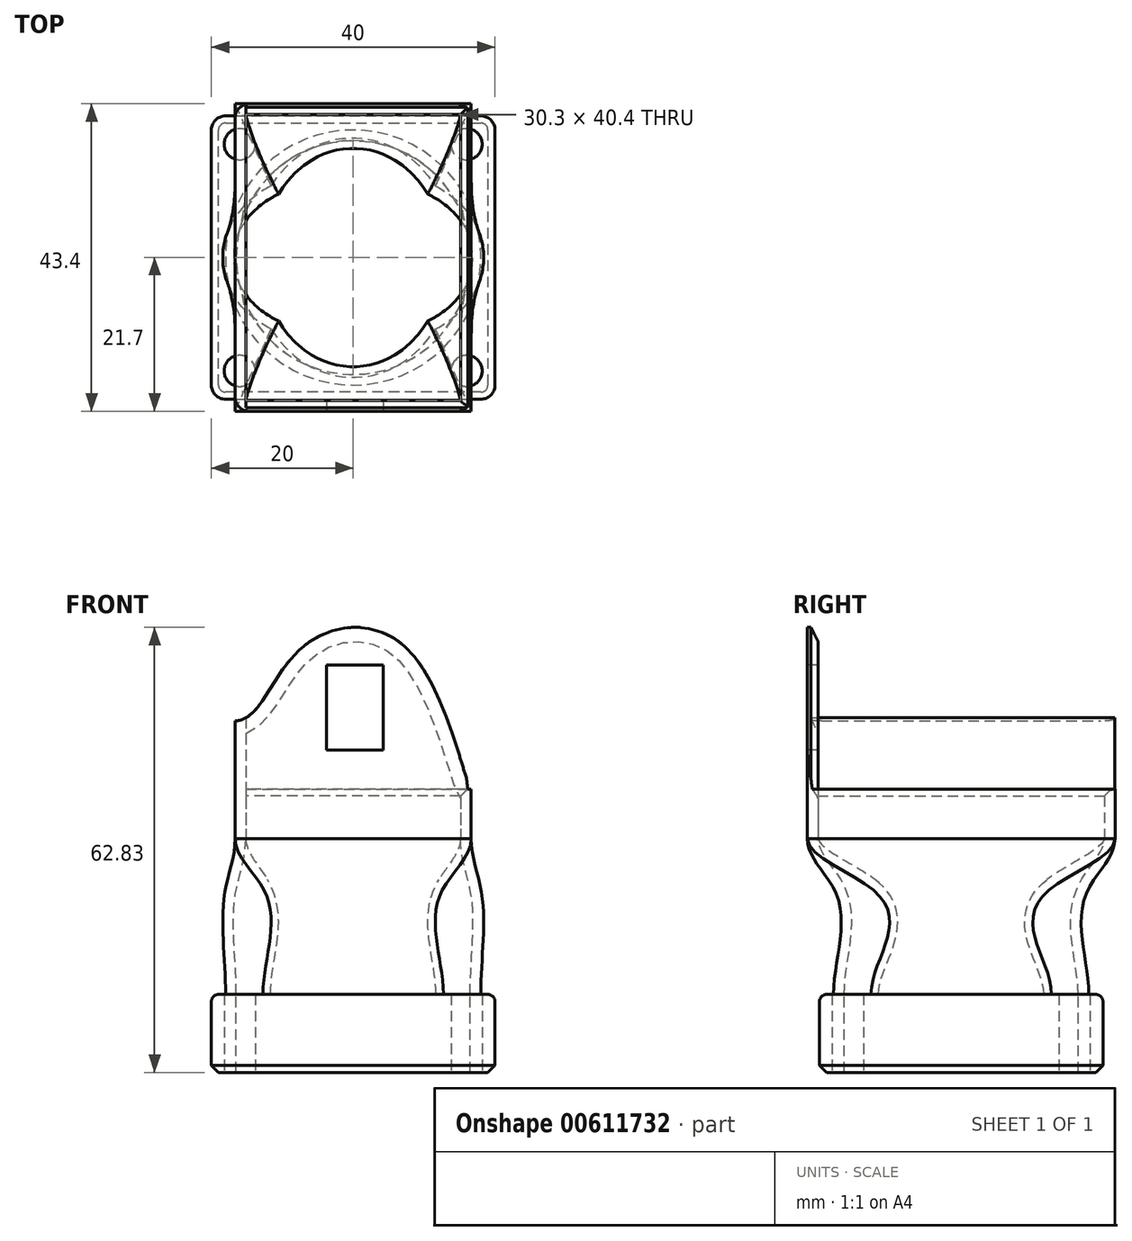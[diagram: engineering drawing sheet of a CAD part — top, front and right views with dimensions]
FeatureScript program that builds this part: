
annotation { "Feature Type Name" : "Feature", "Feature Type Description" : "" }
export const myFeature = defineFeature(function(context is Context, id is Id, definition is map)
    precondition{}
    {
        {
            var Q0;
            Q0=qCreatedBy(makeId("Top.planeOp"),FACE);
            var sketch = newSketch(context, id + "F0", { "sketchPlane" : qUnion([Q0])});
            skLineSegment(sketch, "E0.bottom", {"start": v(-15.15, 20.2) * mm, "end": v(15.15, 20.2) * mm});
            skLineSegment(sketch, "E0.top", {"start": v(-15.15, -20.2) * mm, "end": v(15.15, -20.2) * mm});
            skLineSegment(sketch, "E0.left", {"start": v(-15.15, 20.2) * mm, "end": v(-15.15, -20.2) * mm});
            skLineSegment(sketch, "E0.right", {"start": v(15.15, 20.2) * mm, "end": v(15.15, -20.2) * mm});
            skPoint(sketch, "E0.middle", {"position": v(0, 0) * mm});
            skSolve(sketch);
        }
        {
            var Q0;
            Q0=qCreatedBy(makeId("Top.planeOp"),FACE);
            var sketch = newSketch(context, id + "F1", { "sketchPlane" : qUnion([Q0])});
            skLineSegment(sketch, "E1.0", {"start": v(16.65, 21.7) * mm, "end": v(-16.65, 21.7) * mm});
            skLineSegment(sketch, "E1.1", {"start": v(16.65, -21.7) * mm, "end": v(16.65, 21.7) * mm});
            skLineSegment(sketch, "E1.2", {"start": v(-16.65, -21.7) * mm, "end": v(16.65, -21.7) * mm});
            skLineSegment(sketch, "E1.3", {"start": v(-16.65, 21.7) * mm, "end": v(-16.65, -21.7) * mm});
            skSolve(sketch);
        }
        {
            var Q0;
            Q0=qCreatedBy(makeId("Top.planeOp"),FACE);
            cPlane(context, id + "F2", {"entities" : qUnion([Q0]), "cplaneType" : CPlaneType.OFFSET, "offset" : 22 * mm, "oppositeDirection" : true, "width" : 150 * mm, "height" : 150 * mm});
        }
        {
            var Q0;
            Q0=qCreatedBy(id+"F2.planeOp",FACE);
            var sketch = newSketch(context, id + "F3", { "sketchPlane" : qUnion([Q0])});
            skCircle(sketch, "E2", {"center": v(0, 0) * mm, "radius": 18 * mm});
            skLineSegment(sketch, "E3.bottom", {"start": v(12.73, 12.73) * mm, "end": v(-12.73, 12.73) * mm, "construction": true});
            skLineSegment(sketch, "E3.top", {"start": v(12.73, -12.73) * mm, "end": v(-12.73, -12.73) * mm, "construction": true});
            skLineSegment(sketch, "E3.left", {"start": v(12.73, 12.73) * mm, "end": v(12.73, -12.73) * mm, "construction": true});
            skLineSegment(sketch, "E3.right", {"start": v(-12.73, 12.73) * mm, "end": v(-12.73, -12.73) * mm, "construction": true});
            skSolve(sketch);
        }
        {
            var Q0;
            Q0=qCreatedBy(id+"F2.planeOp",FACE);
            cPlane(context, id + "F4", {"entities" : qUnion([Q0]), "cplaneType" : CPlaneType.OFFSET, "offset" : 15 * mm, "width" : 150 * mm, "height" : 150 * mm});
        }
        {
            var Q0;
            Q0=qCreatedBy(id+"F4.planeOp",FACE);
            var sketch = newSketch(context, id + "F5", { "sketchPlane" : qUnion([Q0])});
            skCircle(sketch, "E4.0", {"center": v(0, 0) * mm, "radius": 18 * mm});
            skLineSegment(sketch, "E5.bottom", {"start": v(12.73, 12.73) * mm, "end": v(-12.73, 12.73) * mm, "construction": true});
            skLineSegment(sketch, "E5.top", {"start": v(12.73, -12.73) * mm, "end": v(-12.73, -12.73) * mm, "construction": true});
            skLineSegment(sketch, "E5.left", {"start": v(12.73, 12.73) * mm, "end": v(12.73, -12.73) * mm, "construction": true});
            skLineSegment(sketch, "E5.right", {"start": v(-12.73, 12.73) * mm, "end": v(-12.73, -12.73) * mm, "construction": true});
            skSolve(sketch);
        }
        {
            var Q0;
            Q0=makeQuery(id+"F1.imprint","IMPRINT",FACE,{"disambiguationData":[TD([[makeQuery(id+"F1.imprint","IMPRINT",EDGE,{"derivedFrom":sQuery(id+"F1.wireOp",EDGE,"E1.0")}),1.0]])]});
            var Q1;
            Q1=makeQuery(id+"F5.imprint","IMPRINT",FACE,{"disambiguationData":[TD([[makeQuery(id+"F5.imprint","IMPRINT",EDGE,{"derivedFrom":sQuery(id+"F5.wireOp",EDGE,"E4.0")}),1.0]])]});
            var Q2;
            Q2=makeQuery(id+"F3.imprint","IMPRINT",FACE,{"disambiguationData":[TD([[makeQuery(id+"F3.imprint","IMPRINT",EDGE,{"derivedFrom":sQuery(id+"F3.wireOp",EDGE,"E2")}),1.0]])]});
            var Q3;
            Q3=sQuery(id+"F1.wireOp",VERTEX,"E1.1.end");
            var Q4;
            Q4=sQuery(id+"F5.wireOp",VERTEX,"E5.bottom.start");
            var Q5;
            Q5=sQuery(id+"F3.wireOp",VERTEX,"E3.left.start");
            loft(context, id + "F6", {"startCondition" : LoftEndDerivativeType.NORMAL_TO_PROFILE, "startMagnitude" : 1, "endCondition" : LoftEndDerivativeType.NORMAL_TO_PROFILE, "endMagnitude" : 1, "sheetProfilesArray" : [{ "sheetProfileEntities" : qUnion([Q0]) }, { "sheetProfileEntities" : qUnion([Q1]) }, { "sheetProfileEntities" : qUnion([Q2]) }], "matchConnections" : true, "connections" : [{ "connectionEntities" : qUnion([Q3, Q4, Q5]), "connectionEdgeQueries" : qUnion([]), "connectionEdgeParameters" : [] }]});
        }
        {
            var Q0;
            Q0=makeQuery(id+"F6.opLoft","CAP_FACE",FACE,{"disambiguationData":[OSD([makeQuery(id+"F1.imprint","IMPRINT",FACE,{"disambiguationData":[TD([[makeQuery(id+"F1.imprint","IMPRINT",EDGE,{"derivedFrom":sQuery(id+"F1.wireOp",EDGE,"E1.0")}),1.0]])]})])],"isStart":true});
            var Q1;
            Q1=makeQuery(id+"F6.opLoft","CAP_FACE",FACE,{"disambiguationData":[OSD([makeQuery(id+"F3.imprint","IMPRINT",FACE,{"disambiguationData":[TD([[makeQuery(id+"F3.imprint","IMPRINT",EDGE,{"derivedFrom":sQuery(id+"F3.wireOp",EDGE,"E2")}),1.0]])]})])],"isStart":true});
            shell(context, id + "F7", {"entities" : qUnion([Q0, Q1]), "thickness" : 1.5 * mm});
        }
        {
            var Q0;
            Q0=qSketchRegion(id+"F1",true);
            extrude(context, id + "F8", {"entities" : qUnion([Q0]), "depth" : 7 * mm});
        }
        {
            var Q0;
            Q0=makeQuery(id+"F8.opExtrude","CAP_FACE",FACE,{"disambiguationData":[OSD([sQuery(id+"F1.wireOp",EDGE,"E1.0"),sQuery(id+"F1.wireOp",EDGE,"E1.1"),sQuery(id+"F1.wireOp",EDGE,"E1.2"),sQuery(id+"F1.wireOp",EDGE,"E1.3")])],"isStart":false});
            var Q1;
            Q1=makeQuery(id+"F8.opExtrude","CAP_FACE",FACE,{"disambiguationData":[OSD([sQuery(id+"F1.wireOp",EDGE,"E1.0"),sQuery(id+"F1.wireOp",EDGE,"E1.1"),sQuery(id+"F1.wireOp",EDGE,"E1.2"),sQuery(id+"F1.wireOp",EDGE,"E1.3")])],"isStart":true});
            shell(context, id + "F9", {"entities" : qUnion([Q0, Q1]), "thickness" : 1.5 * mm});
        }
        {
            var Q0;
            Q0=qCreatedBy(id+"F2.planeOp",FACE);
            var sketch = newSketch(context, id + "F10", { "sketchPlane" : qUnion([Q0])});
            skLineSegment(sketch, "E6.bottom", {"start": v(-20, -20) * mm, "end": v(20, -20) * mm});
            skLineSegment(sketch, "E6.top", {"start": v(-20, 20) * mm, "end": v(20, 20) * mm});
            skLineSegment(sketch, "E6.left", {"start": v(-20, -20) * mm, "end": v(-20, 20) * mm});
            skLineSegment(sketch, "E6.right", {"start": v(20, -20) * mm, "end": v(20, 20) * mm});
            skPoint(sketch, "E6.middle", {"position": v(0, 0) * mm});
            skSolve(sketch);
        }
        {
            var Q0;
            Q0=qSketchRegion(id+"F10",true);
            extrude(context, id + "F11", {"entities" : qUnion([Q0]), "operationType" : NewBodyOperationType.ADD, "oppositeDirection" : true, "depth" : 11 * mm});
        }
        {
            var Q0;
            {var subQ0=sQuery(id+"F5.wireOp",EDGE,"E4.0");var subQ2=sQuery(id+"F1.wireOp",EDGE,"E1.0");var subQ4=sQuery(id+"F1.wireOp",EDGE,"E1.2");var subQ7=sQuery(id+"F1.wireOp",EDGE,"E1.1");Q0=makeQuery(id+"F11.boolean.opBoolean","SPLIT",FACE,{"disambiguationData":[TD([makeQuery(id+"F7.opShell","OFFSET_FACE",FACE,{"disambiguationData":[OSD([subQ2,subQ7,subQ4,subQ0])]})])],"derivedFrom":makeQuery(id+"F11.opExtrude","CAP_FACE",FACE,{"disambiguationData":[OSD([sQuery(id+"F10.wireOp",EDGE,"E6.bottom"),sQuery(id+"F10.wireOp",EDGE,"E6.top"),sQuery(id+"F10.wireOp",EDGE,"E6.left"),sQuery(id+"F10.wireOp",EDGE,"E6.right")])],"isStart":true})});}
            var Q1;
            Q1=makeQuery(id+"F11.opExtrude","CAP_FACE",FACE,{"disambiguationData":[OSD([sQuery(id+"F10.wireOp",EDGE,"E6.bottom"),sQuery(id+"F10.wireOp",EDGE,"E6.top"),sQuery(id+"F10.wireOp",EDGE,"E6.left"),sQuery(id+"F10.wireOp",EDGE,"E6.right")])],"isStart":false});
            extrude(context, id + "F12", {"entities" : qUnion([Q0]), "operationType" : NewBodyOperationType.REMOVE, "endBound" : BoundingType.UP_TO_SURFACE, "oppositeDirection" : true, "endBoundEntityFace" : qUnion([Q1]), "depth" : 25 * mm});
        }
        {
            var Q0;
            Q0=makeQuery(id+"F11.opExtrude","CAP_FACE",FACE,{"disambiguationData":[OSD([sQuery(id+"F10.wireOp",EDGE,"E6.bottom"),sQuery(id+"F10.wireOp",EDGE,"E6.top"),sQuery(id+"F10.wireOp",EDGE,"E6.left"),sQuery(id+"F10.wireOp",EDGE,"E6.right")])],"isStart":false});
            var sketch = newSketch(context, id + "F13", { "sketchPlane" : qUnion([Q0])});
            skLineSegment(sketch, "E7.bottom", {"start": v(16, 16) * mm, "end": v(-16, 16) * mm, "construction": true});
            skLineSegment(sketch, "E7.top", {"start": v(16, -16) * mm, "end": v(-16, -16) * mm, "construction": true});
            skLineSegment(sketch, "E7.left", {"start": v(16, 16) * mm, "end": v(16, -16) * mm, "construction": true});
            skLineSegment(sketch, "E7.right", {"start": v(-16, 16) * mm, "end": v(-16, -16) * mm, "construction": true});
            skPoint(sketch, "E7.middle", {"position": v(0, 0) * mm});
            skSolve(sketch);
        }
        {
            var Q0;
            Q0=sQuery(id+"F13.wireOp",VERTEX,"E7.bottom.end");
            var Q1;
            Q1=sQuery(id+"F13.wireOp",VERTEX,"E7.bottom.start");
            var Q2;
            Q2=sQuery(id+"F13.wireOp",VERTEX,"E7.top.start");
            var Q3;
            Q3=sQuery(id+"F13.wireOp",VERTEX,"E7.top.end");
            var Q4;
            Q4=makeQuery(id+"F6.opLoft","SWEPT_BODY",BODY,{"disambiguationData":[OSD([makeQuery(id+"F1.imprint","IMPRINT",FACE,{"disambiguationData":[TD([[makeQuery(id+"F1.imprint","IMPRINT",EDGE,{"derivedFrom":sQuery(id+"F1.wireOp",EDGE,"E1.0")}),1.0]])]}),makeQuery(id+"F3.imprint","IMPRINT",FACE,{"disambiguationData":[TD([[makeQuery(id+"F3.imprint","IMPRINT",EDGE,{"derivedFrom":sQuery(id+"F3.wireOp",EDGE,"E2")}),1.0]])]}),sQuery(id+"F5.wireOp",EDGE,"E4.0")])]});
            hole(context, id + "F14", {"style" : HoleStyle.SIMPLE, "endStyle" : HoleEndStyle.BLIND, "standardTappedOrClearance" : lookupTablePath({ "standard" : "ISO", "fit" : "Normal", "size" : "M4", "type" : "Clearance" }), "standardBlindInLast" : lookupTablePath({ "fit" : "Standard", "standard" : "ISO", "size" : "M4", "type" : "Clearance" }), "holeDiameter" : 4.4 * mm, "holeDepth" : 20 * mm, "locations" : qUnion([Q0, Q1, Q2, Q3]), "scope" : qUnion([Q4])});
        }
        {
            var Q0;
            Q0=makeQuery(id+"F8.opExtrude","CAP_FACE",FACE,{"disambiguationData":[OSD([sQuery(id+"F1.wireOp",EDGE,"E1.0"),sQuery(id+"F1.wireOp",EDGE,"E1.1"),sQuery(id+"F1.wireOp",EDGE,"E1.2"),sQuery(id+"F1.wireOp",EDGE,"E1.3")])],"isStart":false});
            var sketch = newSketch(context, id + "F15", { "sketchPlane" : qUnion([Q0])});
            skLineSegment(sketch, "E8.0", {"start": v(-16.65, 21.7) * mm, "end": v(-16.65, -21.7) * mm});
            skLineSegment(sketch, "E8.1", {"start": v(-16.65, -21.7) * mm, "end": v(16.65, -21.7) * mm});
            skLineSegment(sketch, "E9", {"start": v(-15.15, 21.7) * mm, "end": v(-15.15, -20.2) * mm});
            skLineSegment(sketch, "E10", {"start": v(-15.15, -20.2) * mm, "end": v(16.65, -20.2) * mm});
            skLineSegment(sketch, "E11", {"start": v(16.65, -20.2) * mm, "end": v(16.65, -21.7) * mm});
            skSolve(sketch);
        }
        {
            var Q0;
            Q0=makeQuery(id+"F8.opExtrude","SWEPT_FACE",FACE,{"disambiguationData":[OSD([sQuery(id+"F1.wireOp",EDGE,"E1.2")])]});
            var sketch = newSketch(context, id + "F16", { "sketchPlane" : qUnion([Q0])});
            skFitSpline(sketch, "E12", {"points": [v(16.65, 7) * mm, v(7.72, 26.7) * mm, v(-7.72, 26.52) * mm, v(-16.65, 16.63) * mm], "startDerivative": vector(-7.54, 7.14) * mm, "endDerivative": vector(-35.64, -0.51) * mm});
            skLineSegment(sketch, "E13.bottom", {"start": v(4.25, 12.5) * mm, "end": v(-3.75, 12.5) * mm});
            skLineSegment(sketch, "E13.top", {"start": v(4.25, 24.5) * mm, "end": v(-3.75, 24.5) * mm});
            skLineSegment(sketch, "E13.left", {"start": v(4.25, 12.5) * mm, "end": v(4.25, 24.5) * mm});
            skLineSegment(sketch, "E13.right", {"start": v(-3.75, 12.5) * mm, "end": v(-3.75, 24.5) * mm});
            skSolve(sketch);
        }
        {
            var Q0;
            Q0=sQuery(id+"F16.wireOp",EDGE,"E12");
            var Q1;
            Q1=makeQuery(id+"F8.opExtrude","SWEPT_FACE",FACE,{"disambiguationData":[OSD([sQuery(id+"F1.wireOp",EDGE,"E1.0")])]});
            extrude(context, id + "F17", {"bodyType" : ToolBodyType.SURFACE, "surfaceEntities" : qUnion([Q0]), "endBound" : BoundingType.UP_TO_SURFACE, "oppositeDirection" : true, "endBoundEntityFace" : qUnion([Q1]), "depth" : 25 * mm});
        }
        {
            var Q0;
            {var subQ7=sQuery(id+"F15.wireOp",EDGE,"E8.0");Q0=makeQuery(id+"F15.imprint","IMPRINT",FACE,{"disambiguationData":[TD([[makeQuery(id+"F15.imprint","IMPRINT",EDGE,{"derivedFrom":subQ7}),1.0]])]});}
            extrude(context, id + "F18", {"entities" : qUnion([Q0]), "operationType" : NewBodyOperationType.ADD, "endBound" : BoundingType.UP_TO_NEXT, "depth" : 25 * mm});
        }
        {
            var Q0;
            Q0=makeQuery(id+"F16.imprint","IMPRINT",FACE,{"disambiguationData":[TD([[makeQuery(id+"F16.imprint","IMPRINT",EDGE,{"derivedFrom":sQuery(id+"F16.wireOp",EDGE,"E13.bottom")}),-1.0]])]});
            extrude(context, id + "F19", {"entities" : qUnion([Q0]), "operationType" : NewBodyOperationType.REMOVE, "endBound" : BoundingType.UP_TO_NEXT, "oppositeDirection" : true, "depth" : 25 * mm});
        }
        {
            var Q0;
            Q0=makeQuery(id+"F11.opExtrude","SWEPT_EDGE",EDGE,{"disambiguationData":[OSD([sQuery(id+"F10.wireOp",EDGE,"E6.bottom"),sQuery(id+"F10.wireOp",EDGE,"E6.left")])]});
            var Q1;
            Q1=makeQuery(id+"F11.opExtrude","SWEPT_EDGE",EDGE,{"disambiguationData":[OSD([sQuery(id+"F10.wireOp",EDGE,"E6.bottom"),sQuery(id+"F10.wireOp",EDGE,"E6.right")])]});
            var Q2;
            Q2=makeQuery(id+"F11.opExtrude","SWEPT_EDGE",EDGE,{"disambiguationData":[OSD([sQuery(id+"F10.wireOp",EDGE,"E6.top"),sQuery(id+"F10.wireOp",EDGE,"E6.left")])]});
            var Q3;
            Q3=makeQuery(id+"F11.opExtrude","SWEPT_EDGE",EDGE,{"disambiguationData":[OSD([sQuery(id+"F10.wireOp",EDGE,"E6.top"),sQuery(id+"F10.wireOp",EDGE,"E6.right")])]});
            var Q4;
            Q4=makeQuery(id+"F8.opExtrude","SWEPT_EDGE",EDGE,{"disambiguationData":[OSD([sQuery(id+"F1.wireOp",EDGE,"E1.0"),sQuery(id+"F1.wireOp",EDGE,"E1.1")])]});
            var Q5;
            Q5=makeQuery(id+"F8.opExtrude","SWEPT_EDGE",EDGE,{"disambiguationData":[OSD([sQuery(id+"F1.wireOp",EDGE,"E1.0"),sQuery(id+"F1.wireOp",EDGE,"E1.3")])]});
            var Q6;
            Q6=makeQuery(id+"F8.opExtrude","SWEPT_EDGE",EDGE,{"disambiguationData":[OSD([sQuery(id+"F1.wireOp",EDGE,"E1.2"),sQuery(id+"F1.wireOp",EDGE,"E1.3")])]});
            var Q7;
            Q7=makeQuery(id+"F8.opExtrude","SWEPT_EDGE",EDGE,{"disambiguationData":[OSD([sQuery(id+"F1.wireOp",EDGE,"E1.1"),sQuery(id+"F1.wireOp",EDGE,"E1.2")])]});
            fillet(context, id + "F20", {"entities" : qUnion([Q0, Q1, Q2, Q3, Q4, Q5, Q6, Q7]), "radius" : 2 * mm, "tangentPropagation" : true, "allowEdgeOverflow" : false});
        }
        {
            var Q0;
            Q0=makeQuery(id+"F8.opExtrude","CAP_EDGE",EDGE,{"disambiguationData":[OSD([sQuery(id+"F1.wireOp",EDGE,"E1.3")])],"isStart":false});
            var Q1;
            Q1=makeQuery(id+"F11.opExtrude","CAP_EDGE",EDGE,{"disambiguationData":[OSD([sQuery(id+"F10.wireOp",EDGE,"E6.left")])],"isStart":true});
            fillet(context, id + "F21", {"entities" : qUnion([Q0, Q1]), "radius" : 1 * mm, "tangentPropagation" : true, "allowEdgeOverflow" : false});
        }
        {
            var Q0;
            Q0=makeQuery(id+"F11.opExtrude","CAP_EDGE",EDGE,{"disambiguationData":[OSD([sQuery(id+"F10.wireOp",EDGE,"E6.left")])],"isStart":false});
            chamfer(context, id + "F22", {"entities" : qUnion([Q0]), "width" : 1 * mm, "tangentPropagation" : true});
        }
        {
            var Q0;
            {var subQ0=sQuery(id+"F1.wireOp",EDGE,"E1.1");Q0=makeQuery(id+"F9.opShell","OFFSET_EDGE",EDGE,{"disambiguationData":[OSD([subQ0]),TDD([makeQuery(id+"F8.opExtrude","CAP_EDGE",EDGE,{"disambiguationData":[OSD([subQ0])],"isStart":false})])]});}
            var Q1;
            {var subQ0=sQuery(id+"F1.wireOp",EDGE,"E1.0");Q1=makeQuery(id+"F9.opShell","OFFSET_EDGE",EDGE,{"disambiguationData":[OSD([subQ0]),TDD([makeQuery(id+"F8.opExtrude","CAP_EDGE",EDGE,{"disambiguationData":[OSD([subQ0])],"isStart":false})])]});}
            var Q2;
            {var subQ0=sQuery(id+"F15.wireOp",EDGE,"E9");var subQ1=sQuery(id+"F1.wireOp",EDGE,"E1.0");var subQ2=makeQuery(id+"F8.opExtrude","CAP_EDGE",EDGE,{"disambiguationData":[OSD([subQ1])],"isStart":false});Q2=makeQuery(id+"F18.opExtrude","TWEAK_EDGE",EDGE,{"derivedFrom":[makeQuery(id+"F15.imprint","IMPRINT",EDGE,{"disambiguationData":[TD([[makeQuery(id+"F15.imprint","INTERSECT",VERTEX,{"derivedFrom":[subQ2,subQ0]}),-1.0]])],"derivedFrom":subQ0}),makeQuery(id+"F15.imprint","IMPRINT",EDGE,{"disambiguationData":[TD([[makeQuery(id+"F15.imprint","INTERSECT",VERTEX,{"derivedFrom":[subQ0,sQuery(id+"F15.wireOp",EDGE,"E10")]}),1.0]])],"derivedFrom":subQ0}),makeQuery(id+"F17.opExtrude","SWEPT_FACE",FACE,{"disambiguationData":[OSD([sQuery(id+"F16.wireOp",EDGE,"E12")])]})]});}
            chamfer(context, id + "F23", {"entities" : qUnion([Q0, Q1, Q2]), "width" : 1 * mm, "tangentPropagation" : true});
        }
        {
            var Q0;
            {var subQ0=sQuery(id+"F15.wireOp",EDGE,"E10");var subQ1=sQuery(id+"F1.wireOp",EDGE,"E1.1");var subQ2=makeQuery(id+"F8.opExtrude","CAP_EDGE",EDGE,{"disambiguationData":[OSD([subQ1])],"isStart":false});var subQ3=makeQuery(id+"F15.imprint","INTERSECT",VERTEX,{"derivedFrom":[makeQuery(id+"F9.opShell","OFFSET_EDGE",EDGE,{"disambiguationData":[OSD([subQ1]),TDD([subQ2])]}),subQ0]});Q0=makeQuery(id+"F18.opExtrude","TWEAK_EDGE",EDGE,{"derivedFrom":[makeQuery(id+"F15.imprint","IMPRINT",EDGE,{"disambiguationData":[TD([[makeQuery(id+"F15.imprint","INTERSECT",VERTEX,{"derivedFrom":[sQuery(id+"F15.wireOp",EDGE,"E9"),subQ0]}),-1.0]])],"derivedFrom":subQ0}),makeQuery(id+"F15.imprint","IMPRINT",EDGE,{"disambiguationData":[TD([[subQ3,-1.0]])],"derivedFrom":subQ0}),makeQuery(id+"F17.opExtrude","SWEPT_FACE",FACE,{"disambiguationData":[OSD([sQuery(id+"F16.wireOp",EDGE,"E12")])]})]});}
            chamfer(context, id + "F24", {"entities" : qUnion([Q0]), "chamferType" : ChamferType.TWO_OFFSETS, "width1" : 1 * mm, "oppositeDirection" : false, "width2" : 2 * mm, "tangentPropagation" : true});
        }
    });
